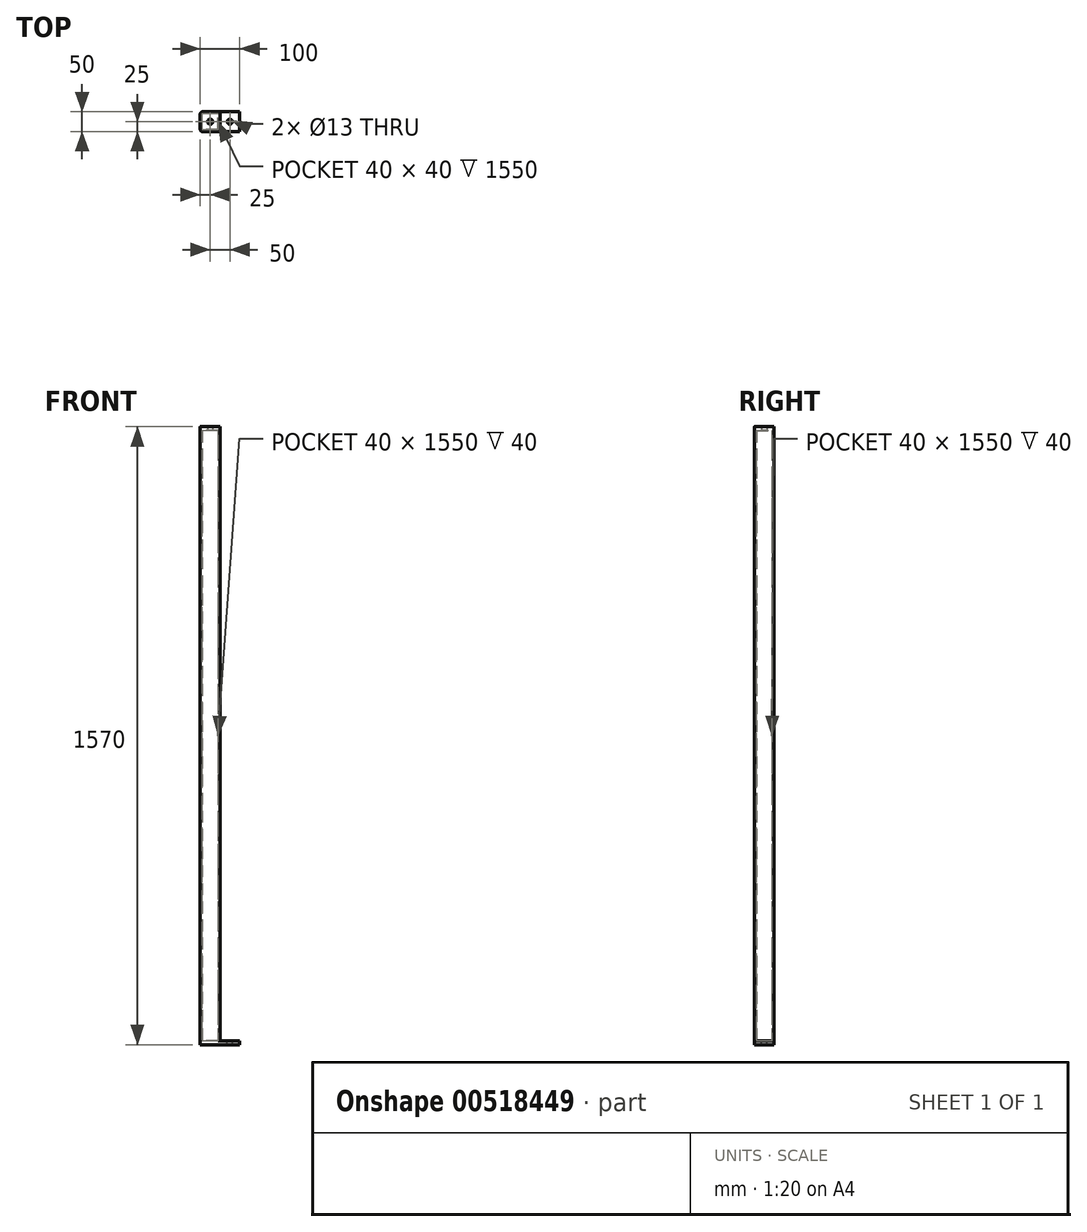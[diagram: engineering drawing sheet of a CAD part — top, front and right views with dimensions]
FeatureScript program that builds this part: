
annotation { "Feature Type Name" : "Feature", "Feature Type Description" : "" }
export const myFeature = defineFeature(function(context is Context, id is Id, definition is map)
    precondition{}
    {
        {
            var Q0;
            Q0=qCreatedBy(makeId("Top.planeOp"),FACE);
            var sketch = newSketch(context, id + "F0", { "sketchPlane" : qUnion([Q0])});
            skLineSegment(sketch, "E0.bottom", {"start": v(20, -25) * mm, "end": v(-20, -25) * mm});
            skLineSegment(sketch, "E0.top", {"start": v(20, 25) * mm, "end": v(-20, 25) * mm});
            skLineSegment(sketch, "E0.left", {"start": v(25, -20) * mm, "end": v(25, 20) * mm});
            skLineSegment(sketch, "E0.right", {"start": v(-25, -20) * mm, "end": v(-25, 20) * mm});
            skPoint(sketch, "E0.middle", {"position": v(0, 0) * mm});
            skLineSegment(sketch, "E1.bottom", {"start": v(20, -20) * mm, "end": v(-20, -20) * mm});
            skLineSegment(sketch, "E1.top", {"start": v(20, 20) * mm, "end": v(-20, 20) * mm});
            skLineSegment(sketch, "E1.left", {"start": v(20, -20) * mm, "end": v(20, 20) * mm});
            skLineSegment(sketch, "E1.right", {"start": v(-20, -20) * mm, "end": v(-20, 20) * mm});
            skPoint(sketch, "E2.visualSharp", {"position": v(-25, 25) * mm});
            skArc(sketch, "E2.filletArc", {"start": v(-20, 25) * mm, "mid": v(-23.54, 23.54) * mm, "end": v(-25, 20) * mm});
            skPoint(sketch, "E3.visualSharp", {"position": v(25, 25) * mm});
            skArc(sketch, "E3.filletArc", {"start": v(25, 20) * mm, "mid": v(23.54, 23.54) * mm, "end": v(20, 25) * mm});
            skPoint(sketch, "E4.visualSharp", {"position": v(-25, -25) * mm});
            skArc(sketch, "E4.filletArc", {"start": v(-25, -20) * mm, "mid": v(-23.54, -23.54) * mm, "end": v(-20, -25) * mm});
            skPoint(sketch, "E5.visualSharp", {"position": v(25, -25) * mm});
            skArc(sketch, "E5.filletArc", {"start": v(20, -25) * mm, "mid": v(23.54, -23.54) * mm, "end": v(25, -20) * mm});
            skSolve(sketch);
        }
        {
            var Q0;
            Q0=qSketchRegion(id+"F0",true);
            extrude(context, id + "F1", {"entities" : qUnion([Q0]), "depth" : 1550 * mm, "offsetDistance" : 25 * mm});
        }
        {
            var Q0;
            Q0=makeQuery(id+"F1.opExtrude","CAP_FACE",FACE,{"disambiguationData":[OSD([sQuery(id+"F0.wireOp",EDGE,"E0.bottom"),sQuery(id+"F0.wireOp",EDGE,"E0.top"),sQuery(id+"F0.wireOp",EDGE,"E0.left"),sQuery(id+"F0.wireOp",EDGE,"E0.right"),sQuery(id+"F0.wireOp",EDGE,"E1.bottom"),sQuery(id+"F0.wireOp",EDGE,"E1.top"),sQuery(id+"F0.wireOp",EDGE,"E1.left"),sQuery(id+"F0.wireOp",EDGE,"E1.right"),sQuery(id+"F0.wireOp",EDGE,"E2.filletArc"),sQuery(id+"F0.wireOp",EDGE,"E3.filletArc"),sQuery(id+"F0.wireOp",EDGE,"E4.filletArc"),sQuery(id+"F0.wireOp",EDGE,"E5.filletArc")])],"isStart":false});
            var sketch = newSketch(context, id + "F2", { "sketchPlane" : qUnion([Q0])});
            skArc(sketch, "E6.0", {"start": v(-20, 25) * mm, "mid": v(-23.54, 23.54) * mm, "end": v(-25, 20) * mm});
            skArc(sketch, "E6.1", {"start": v(25, 20) * mm, "mid": v(23.54, 23.54) * mm, "end": v(20, 25) * mm});
            skArc(sketch, "E6.2", {"start": v(20, -25) * mm, "mid": v(23.54, -23.54) * mm, "end": v(25, -20) * mm});
            skArc(sketch, "E7.0", {"start": v(-25, -20) * mm, "mid": v(-23.54, -23.54) * mm, "end": v(-20, -25) * mm});
            skLineSegment(sketch, "E8.0", {"start": v(-25, -20) * mm, "end": v(-25, 20) * mm});
            skLineSegment(sketch, "E9.0", {"start": v(-20, -20) * mm, "end": v(-20, 20) * mm});
            skLineSegment(sketch, "E10.0", {"start": v(20, 20) * mm, "end": v(-20, 20) * mm});
            skLineSegment(sketch, "E11.0", {"start": v(20, 25) * mm, "end": v(-20, 25) * mm});
            skLineSegment(sketch, "E12.0", {"start": v(25, -20) * mm, "end": v(25, 20) * mm});
            skLineSegment(sketch, "E13.0", {"start": v(20, -25) * mm, "end": v(-20, -25) * mm});
            skCircle(sketch, "E14", {"center": v(0, 0) * mm, "radius": 6.5 * mm});
            skSolve(sketch);
        }
        {
            var Q0;
            Q0=qSketchRegion(id+"F2",true);
            extrude(context, id + "F3", {"entities" : qUnion([Q0]), "operationType" : NewBodyOperationType.ADD, "depth" : 10 * mm, "offsetDistance" : 25 * mm});
        }
        {
            var Q0;
            Q0=makeQuery(id+"F1.opExtrude","CAP_FACE",FACE,{"disambiguationData":[OSD([sQuery(id+"F0.wireOp",EDGE,"E0.bottom"),sQuery(id+"F0.wireOp",EDGE,"E0.top"),sQuery(id+"F0.wireOp",EDGE,"E0.left"),sQuery(id+"F0.wireOp",EDGE,"E0.right"),sQuery(id+"F0.wireOp",EDGE,"E1.bottom"),sQuery(id+"F0.wireOp",EDGE,"E1.top"),sQuery(id+"F0.wireOp",EDGE,"E1.left"),sQuery(id+"F0.wireOp",EDGE,"E1.right"),sQuery(id+"F0.wireOp",EDGE,"E2.filletArc"),sQuery(id+"F0.wireOp",EDGE,"E3.filletArc"),sQuery(id+"F0.wireOp",EDGE,"E4.filletArc"),sQuery(id+"F0.wireOp",EDGE,"E5.filletArc")])],"isStart":true});
            var sketch = newSketch(context, id + "F4", { "sketchPlane" : qUnion([Q0])});
            skArc(sketch, "E15.1", {"start": v(-25, 20) * mm, "mid": v(-23.54, 23.54) * mm, "end": v(-20, 25) * mm});
            skLineSegment(sketch, "E16", {"start": v(-20, 25) * mm, "end": v(75, 25) * mm});
            skLineSegment(sketch, "E17", {"start": v(75, 25) * mm, "end": v(75, -25) * mm});
            skCircle(sketch, "E18", {"center": v(50, 0) * mm, "radius": 6.5 * mm});
            skLineSegment(sketch, "E19", {"start": v(75, -25) * mm, "end": v(-20, -25) * mm});
            skPoint(sketch, "E19.endSnap0", {"position": v(0, -25) * mm});
            skLineSegment(sketch, "E20", {"start": v(-25, -20) * mm, "end": v(-25, 20) * mm});
            skPoint(sketch, "E21.visualSharp", {"position": v(-25, -25) * mm});
            skArc(sketch, "E21.filletArc", {"start": v(-25, -20) * mm, "mid": v(-23.54, -23.54) * mm, "end": v(-20, -25) * mm});
            skSolve(sketch);
        }
        {
            var Q0;
            Q0=qSketchRegion(id+"F4",true);
            extrude(context, id + "F5", {"entities" : qUnion([Q0]), "operationType" : NewBodyOperationType.ADD, "depth" : 10 * mm, "offsetDistance" : 25 * mm});
        }
    });
